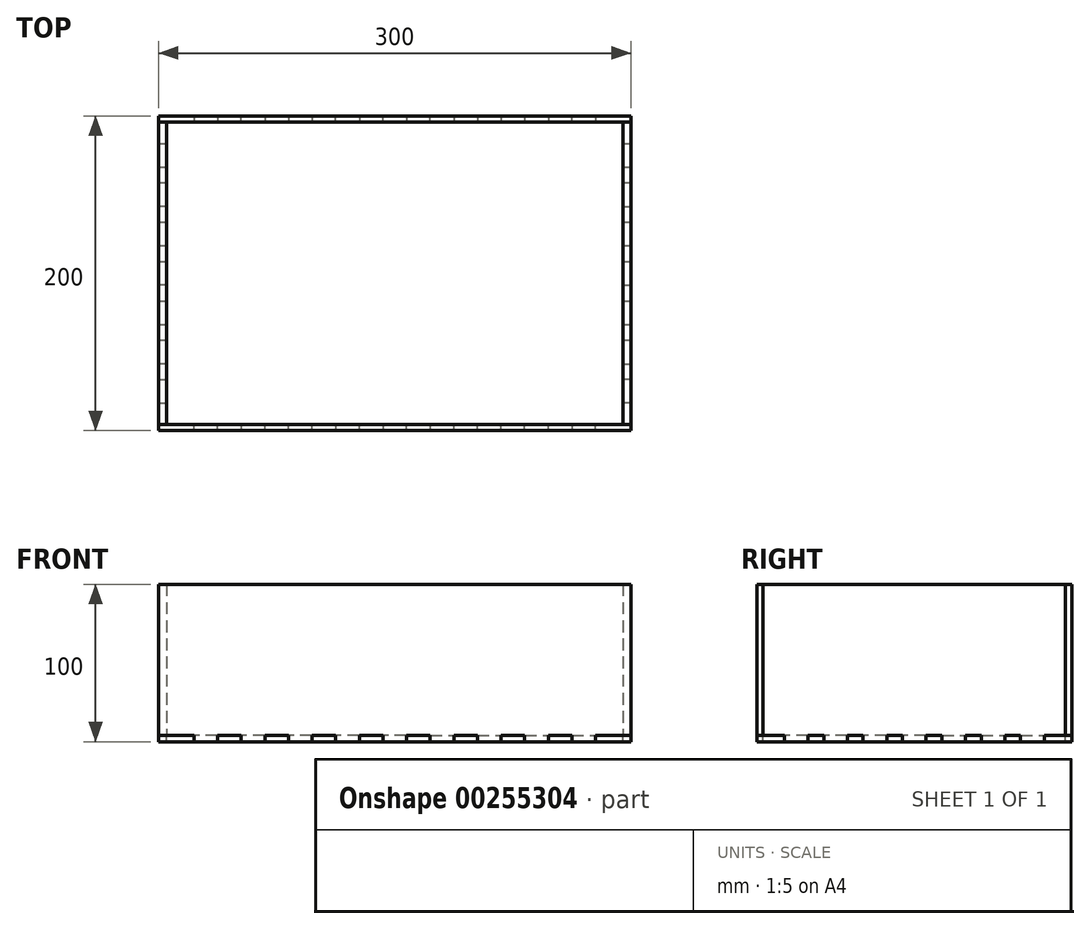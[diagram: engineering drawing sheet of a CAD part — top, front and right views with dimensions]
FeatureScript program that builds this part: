
annotation { "Feature Type Name" : "Feature", "Feature Type Description" : "" }
export const myFeature = defineFeature(function(context is Context, id is Id, definition is map)
    precondition{}
    {
        {
            var Q0;
            Q0=qCreatedBy(makeId("Top.planeOp"),FACE);
            var sketch = newSketch(context, id + "F0", { "sketchPlane" : qUnion([Q0])});
            skLineSegment(sketch, "E0.bottom", {"start": v(150, -100) * mm, "end": v(-150, -100) * mm});
            skLineSegment(sketch, "E0.top", {"start": v(150, 100) * mm, "end": v(-150, 100) * mm});
            skLineSegment(sketch, "E0.left", {"start": v(150, -100) * mm, "end": v(150, 100) * mm});
            skLineSegment(sketch, "E0.right", {"start": v(-150, -100) * mm, "end": v(-150, 100) * mm});
            skPoint(sketch, "E0.middle", {"position": v(0, 0) * mm});
            skLineSegment(sketch, "E1", {"start": v(0, 96) * mm, "end": v(7.5, 96) * mm});
            skLineSegment(sketch, "E2", {"start": v(7.5, 96) * mm, "end": v(7.5, 100) * mm});
            skLineSegment(sketch, "E3", {"start": v(0, 96) * mm, "end": v(-7.5, 96) * mm});
            skLineSegment(sketch, "E4", {"start": v(-7.5, 96) * mm, "end": v(-7.5, 100) * mm});
            skLineSegment(sketch, "E5", {"start": v(-7.5, 96) * mm, "end": v(7.5, 96) * mm});
            skPoint(sketch, "E6.start.orphan", {"position": v(0, 100) * mm});
            skLineSegment(sketch, "E7.1.0.0", {"start": v(22.5, 96) * mm, "end": v(22.5, 100) * mm});
            skLineSegment(sketch, "E7.1.0.1", {"start": v(22.5, 96) * mm, "end": v(37.5, 96) * mm});
            skLineSegment(sketch, "E7.1.0.2", {"start": v(37.5, 96) * mm, "end": v(37.5, 100) * mm});
            skLineSegment(sketch, "E7.2.0.0", {"start": v(52.5, 96) * mm, "end": v(52.5, 100) * mm});
            skLineSegment(sketch, "E7.2.0.1", {"start": v(52.5, 96) * mm, "end": v(67.5, 96) * mm});
            skLineSegment(sketch, "E7.2.0.2", {"start": v(67.5, 96) * mm, "end": v(67.5, 100) * mm});
            skLineSegment(sketch, "E7.3.0.0", {"start": v(82.5, 96) * mm, "end": v(82.5, 100) * mm});
            skLineSegment(sketch, "E7.3.0.1", {"start": v(82.5, 96) * mm, "end": v(97.5, 96) * mm});
            skLineSegment(sketch, "E7.3.0.2", {"start": v(97.5, 96) * mm, "end": v(97.5, 100) * mm});
            skLineSegment(sketch, "E7.4.0.0", {"start": v(112.5, 96) * mm, "end": v(112.5, 100) * mm});
            skLineSegment(sketch, "E7.4.0.1", {"start": v(112.5, 96) * mm, "end": v(127.5, 96) * mm});
            skLineSegment(sketch, "E7.4.0.2", {"start": v(127.5, 96) * mm, "end": v(127.5, 100) * mm});
            skLineSegment(sketch, "E7.direction1", {"start": v(-7.5, 96) * mm, "end": v(22.5, 96) * mm, "construction": true});
            skLineSegment(sketch, "E8.MirrorCS", {"start": v(-97.5, 96) * mm, "end": v(-97.5, 100) * mm});
            skLineSegment(sketch, "E9.MirrorCS", {"start": v(-67.5, 96) * mm, "end": v(-67.5, 100) * mm});
            skLineSegment(sketch, "E10.MirrorCS", {"start": v(-82.5, 96) * mm, "end": v(-82.5, 100) * mm});
            skLineSegment(sketch, "E11.MirrorCS", {"start": v(7.5, 96) * mm, "end": v(-7.5, 96) * mm});
            skLineSegment(sketch, "E12.MirrorCS", {"start": v(-22.5, 96) * mm, "end": v(-22.5, 100) * mm});
            skLineSegment(sketch, "E13.MirrorCS", {"start": v(-37.5, 96) * mm, "end": v(-37.5, 100) * mm});
            skLineSegment(sketch, "E14.MirrorCS", {"start": v(-52.5, 96) * mm, "end": v(-52.5, 100) * mm});
            skLineSegment(sketch, "E15.MirrorCS", {"start": v(-127.5, 96) * mm, "end": v(-127.5, 100) * mm});
            skLineSegment(sketch, "E16.MirrorCS", {"start": v(-112.5, 96) * mm, "end": v(-112.5, 100) * mm});
            skLineSegment(sketch, "E17.MirrorCS", {"start": v(-112.5, 96) * mm, "end": v(-127.5, 96) * mm});
            skLineSegment(sketch, "E18.MirrorCS", {"start": v(-52.5, 96) * mm, "end": v(-67.5, 96) * mm});
            skLineSegment(sketch, "E19.MirrorCS", {"start": v(7.5, 96) * mm, "end": v(-22.5, 96) * mm, "construction": true});
            skLineSegment(sketch, "E20.MirrorCS", {"start": v(-22.5, 96) * mm, "end": v(-37.5, 96) * mm});
            skLineSegment(sketch, "E21.MirrorCS", {"start": v(-82.5, 96) * mm, "end": v(-97.5, 96) * mm});
            skLineSegment(sketch, "E22.MirrorCS", {"start": v(0, -96) * mm, "end": v(-7.5, -96) * mm});
            skLineSegment(sketch, "E23.MirrorCS", {"start": v(0, -96) * mm, "end": v(7.5, -96) * mm});
            skLineSegment(sketch, "E24.MirrorCS", {"start": v(-7.5, -96) * mm, "end": v(7.5, -96) * mm});
            skLineSegment(sketch, "E25.MirrorCS", {"start": v(7.5, -96) * mm, "end": v(-7.5, -96) * mm});
            skLineSegment(sketch, "E26.MirrorCS", {"start": v(-7.5, -96) * mm, "end": v(-7.5, -100) * mm});
            skLineSegment(sketch, "E27.MirrorCS", {"start": v(7.5, -96) * mm, "end": v(7.5, -100) * mm});
            skLineSegment(sketch, "E28.MirrorCS", {"start": v(127.5, -96) * mm, "end": v(127.5, -100) * mm});
            skLineSegment(sketch, "E29.MirrorCS", {"start": v(52.5, -96) * mm, "end": v(52.5, -100) * mm});
            skLineSegment(sketch, "E30.MirrorCS", {"start": v(67.5, -96) * mm, "end": v(67.5, -100) * mm});
            skLineSegment(sketch, "E31.MirrorCS", {"start": v(82.5, -96) * mm, "end": v(82.5, -100) * mm});
            skLineSegment(sketch, "E32.MirrorCS", {"start": v(37.5, -96) * mm, "end": v(37.5, -100) * mm});
            skLineSegment(sketch, "E33.MirrorCS", {"start": v(-82.5, -96) * mm, "end": v(-82.5, -100) * mm});
            skLineSegment(sketch, "E34.MirrorCS", {"start": v(22.5, -96) * mm, "end": v(22.5, -100) * mm});
            skLineSegment(sketch, "E35.MirrorCS", {"start": v(-52.5, -96) * mm, "end": v(-52.5, -100) * mm});
            skPoint(sketch, "E36.MirrorP", {"position": v(0, -100) * mm});
            skLineSegment(sketch, "E37.MirrorCS", {"start": v(-97.5, -96) * mm, "end": v(-97.5, -100) * mm});
            skLineSegment(sketch, "E38.MirrorCS", {"start": v(-22.5, -96) * mm, "end": v(-22.5, -100) * mm});
            skLineSegment(sketch, "E39.MirrorCS", {"start": v(97.5, -96) * mm, "end": v(97.5, -100) * mm});
            skLineSegment(sketch, "E40.MirrorCS", {"start": v(-127.5, -96) * mm, "end": v(-127.5, -100) * mm});
            skLineSegment(sketch, "E41.MirrorCS", {"start": v(-67.5, -96) * mm, "end": v(-67.5, -100) * mm});
            skLineSegment(sketch, "E42.MirrorCS", {"start": v(-37.5, -96) * mm, "end": v(-37.5, -100) * mm});
            skLineSegment(sketch, "E43.MirrorCS", {"start": v(112.5, -96) * mm, "end": v(112.5, -100) * mm});
            skLineSegment(sketch, "E44.MirrorCS", {"start": v(-112.5, -96) * mm, "end": v(-112.5, -100) * mm});
            skLineSegment(sketch, "E45.MirrorCS", {"start": v(52.5, -96) * mm, "end": v(67.5, -96) * mm});
            skLineSegment(sketch, "E46.MirrorCS", {"start": v(-112.5, -96) * mm, "end": v(-127.5, -96) * mm});
            skLineSegment(sketch, "E47.MirrorCS", {"start": v(112.5, -96) * mm, "end": v(127.5, -96) * mm});
            skLineSegment(sketch, "E48.MirrorCS", {"start": v(-82.5, -96) * mm, "end": v(-97.5, -96) * mm});
            skLineSegment(sketch, "E49.MirrorCS", {"start": v(22.5, -96) * mm, "end": v(37.5, -96) * mm});
            skLineSegment(sketch, "E50.MirrorCS", {"start": v(-52.5, -96) * mm, "end": v(-67.5, -96) * mm});
            skLineSegment(sketch, "E51.MirrorCS", {"start": v(82.5, -96) * mm, "end": v(97.5, -96) * mm});
            skLineSegment(sketch, "E52.MirrorCS", {"start": v(-7.5, -96) * mm, "end": v(22.5, -96) * mm, "construction": true});
            skLineSegment(sketch, "E53.MirrorCS", {"start": v(7.5, -96) * mm, "end": v(-22.5, -96) * mm, "construction": true});
            skLineSegment(sketch, "E54.MirrorCS", {"start": v(-22.5, -96) * mm, "end": v(-37.5, -96) * mm});
            skLineSegment(sketch, "E55", {"start": v(-150, 0) * mm, "end": v(-146, 0) * mm});
            skPoint(sketch, "E55.endSnap0", {"position": v(-150, 0) * mm});
            skLineSegment(sketch, "E56", {"start": v(-145, 7.5) * mm, "end": v(-150, 7.5) * mm});
            skLineSegment(sketch, "E57", {"start": v(-145, -7.5) * mm, "end": v(-150, -7.5) * mm});
            skLineSegment(sketch, "E58", {"start": v(-145, -7.5) * mm, "end": v(-145, 7.5) * mm});
            skLineSegment(sketch, "E59.0.1.0", {"start": v(-145, 17.5) * mm, "end": v(-150, 17.5) * mm});
            skLineSegment(sketch, "E59.0.1.1", {"start": v(-145, 17.5) * mm, "end": v(-145, 32.5) * mm});
            skLineSegment(sketch, "E59.0.1.2", {"start": v(-145, 32.5) * mm, "end": v(-150, 32.5) * mm});
            skLineSegment(sketch, "E59.0.2.0", {"start": v(-145, 42.5) * mm, "end": v(-150, 42.5) * mm});
            skLineSegment(sketch, "E59.0.2.1", {"start": v(-145, 42.5) * mm, "end": v(-145, 57.5) * mm});
            skLineSegment(sketch, "E59.0.2.2", {"start": v(-145, 57.5) * mm, "end": v(-150, 57.5) * mm});
            skLineSegment(sketch, "E59.0.3.0", {"start": v(-145, 67.5) * mm, "end": v(-150, 67.5) * mm});
            skLineSegment(sketch, "E59.0.3.1", {"start": v(-145, 67.5) * mm, "end": v(-145, 82.5) * mm});
            skLineSegment(sketch, "E59.0.3.2", {"start": v(-145, 82.5) * mm, "end": v(-150, 82.5) * mm});
            skLineSegment(sketch, "E59.direction1", {"start": v(-150, -7.5) * mm, "end": v(-125, -7.5) * mm, "construction": true});
            skLineSegment(sketch, "E59.direction2", {"start": v(-150, -7.5) * mm, "end": v(-150, 17.5) * mm, "construction": true});
            skLineSegment(sketch, "E60.MirrorCS", {"start": v(-145, -17.5) * mm, "end": v(-150, -17.5) * mm});
            skLineSegment(sketch, "E61.MirrorCS", {"start": v(-145, -67.5) * mm, "end": v(-150, -67.5) * mm});
            skLineSegment(sketch, "E62.MirrorCS", {"start": v(-145, -57.5) * mm, "end": v(-150, -57.5) * mm});
            skLineSegment(sketch, "E63.MirrorCS", {"start": v(-145, -82.5) * mm, "end": v(-150, -82.5) * mm});
            skLineSegment(sketch, "E64.MirrorCS", {"start": v(-145, -42.5) * mm, "end": v(-150, -42.5) * mm});
            skLineSegment(sketch, "E65.MirrorCS", {"start": v(-145, -32.5) * mm, "end": v(-150, -32.5) * mm});
            skLineSegment(sketch, "E66.MirrorCS", {"start": v(-145, 7.5) * mm, "end": v(-145, -7.5) * mm});
            skLineSegment(sketch, "E67.MirrorCS", {"start": v(-145, -17.5) * mm, "end": v(-145, -32.5) * mm});
            skLineSegment(sketch, "E68.MirrorCS", {"start": v(-145, -67.5) * mm, "end": v(-145, -82.5) * mm});
            skLineSegment(sketch, "E69.MirrorCS", {"start": v(-150, 7.5) * mm, "end": v(-150, -17.5) * mm, "construction": true});
            skLineSegment(sketch, "E70.MirrorCS", {"start": v(-145, -42.5) * mm, "end": v(-145, -57.5) * mm});
            skLineSegment(sketch, "E71.MirrorCS", {"start": v(145, -7.5) * mm, "end": v(150, -7.5) * mm});
            skLineSegment(sketch, "E72.MirrorCS", {"start": v(145, 7.5) * mm, "end": v(150, 7.5) * mm});
            skLineSegment(sketch, "E73.MirrorCS", {"start": v(145, 7.5) * mm, "end": v(145, -7.5) * mm});
            skLineSegment(sketch, "E74.MirrorCS", {"start": v(150, 0) * mm, "end": v(146, 0) * mm});
            skLineSegment(sketch, "E75.MirrorCS", {"start": v(145, -7.5) * mm, "end": v(145, 7.5) * mm});
            skLineSegment(sketch, "E76.MirrorCS", {"start": v(145, -17.5) * mm, "end": v(150, -17.5) * mm});
            skLineSegment(sketch, "E77.MirrorCS", {"start": v(145, 17.5) * mm, "end": v(150, 17.5) * mm});
            skLineSegment(sketch, "E78.MirrorCS", {"start": v(145, 57.5) * mm, "end": v(150, 57.5) * mm});
            skLineSegment(sketch, "E79.MirrorCS", {"start": v(145, 67.5) * mm, "end": v(150, 67.5) * mm});
            skLineSegment(sketch, "E80.MirrorCS", {"start": v(145, -67.5) * mm, "end": v(150, -67.5) * mm});
            skLineSegment(sketch, "E81.MirrorCS", {"start": v(145, 82.5) * mm, "end": v(150, 82.5) * mm});
            skLineSegment(sketch, "E82.MirrorCS", {"start": v(145, -57.5) * mm, "end": v(150, -57.5) * mm});
            skPoint(sketch, "E83.MirrorP", {"position": v(150, 0) * mm});
            skLineSegment(sketch, "E84.MirrorCS", {"start": v(145, 42.5) * mm, "end": v(150, 42.5) * mm});
            skLineSegment(sketch, "E85.MirrorCS", {"start": v(145, -32.5) * mm, "end": v(150, -32.5) * mm});
            skLineSegment(sketch, "E86.MirrorCS", {"start": v(145, 32.5) * mm, "end": v(150, 32.5) * mm});
            skLineSegment(sketch, "E87.MirrorCS", {"start": v(145, -42.5) * mm, "end": v(150, -42.5) * mm});
            skLineSegment(sketch, "E88.MirrorCS", {"start": v(145, -82.5) * mm, "end": v(150, -82.5) * mm});
            skLineSegment(sketch, "E89.MirrorCS", {"start": v(145, -42.5) * mm, "end": v(145, -57.5) * mm});
            skLineSegment(sketch, "E90.MirrorCS", {"start": v(145, -17.5) * mm, "end": v(145, -32.5) * mm});
            skLineSegment(sketch, "E91.MirrorCS", {"start": v(145, 42.5) * mm, "end": v(145, 57.5) * mm});
            skLineSegment(sketch, "E92.MirrorCS", {"start": v(145, -67.5) * mm, "end": v(145, -82.5) * mm});
            skLineSegment(sketch, "E93.MirrorCS", {"start": v(150, 7.5) * mm, "end": v(150, -17.5) * mm, "construction": true});
            skLineSegment(sketch, "E94.MirrorCS", {"start": v(145, 67.5) * mm, "end": v(145, 82.5) * mm});
            skLineSegment(sketch, "E95.MirrorCS", {"start": v(150, -7.5) * mm, "end": v(150, 17.5) * mm, "construction": true});
            skLineSegment(sketch, "E96.MirrorCS", {"start": v(145, 17.5) * mm, "end": v(145, 32.5) * mm});
            skSolve(sketch);
        }
        {
            var Q0;
            {var subQ54=sQuery(id+"F0.wireOp",EDGE,"E7.1.0.0");Q0=makeQuery(id+"F0.imprint","IMPRINT",FACE,{"disambiguationData":[TD([[makeQuery(id+"F0.imprint","IMPRINT",EDGE,{"derivedFrom":subQ54}),1.0]])]});}
            extrude(context, id + "F1", {"entities" : qUnion([Q0]), "depth" : 4 * mm});
        }
        {
            var Q0;
            Q0=makeQuery(id+"F1.opExtrude","CAP_FACE",FACE,{"disambiguationData":[OSD([sQuery(id+"F0.wireOp",EDGE,"E0.bottom"),sQuery(id+"F0.wireOp",EDGE,"E0.top"),sQuery(id+"F0.wireOp",EDGE,"E0.left"),sQuery(id+"F0.wireOp",EDGE,"E0.right"),sQuery(id+"F0.wireOp",EDGE,"E7.1.0.0"),sQuery(id+"F0.wireOp",EDGE,"E7.1.0.1"),sQuery(id+"F0.wireOp",EDGE,"E7.1.0.2"),sQuery(id+"F0.wireOp",EDGE,"E7.2.0.0"),sQuery(id+"F0.wireOp",EDGE,"E7.2.0.1"),sQuery(id+"F0.wireOp",EDGE,"E7.2.0.2"),sQuery(id+"F0.wireOp",EDGE,"E7.3.0.0"),sQuery(id+"F0.wireOp",EDGE,"E7.3.0.1"),sQuery(id+"F0.wireOp",EDGE,"E7.3.0.2"),sQuery(id+"F0.wireOp",EDGE,"E7.4.0.0"),sQuery(id+"F0.wireOp",EDGE,"E7.4.0.1"),sQuery(id+"F0.wireOp",EDGE,"E7.4.0.2"),sQuery(id+"F0.wireOp",EDGE,"E8.MirrorCS"),sQuery(id+"F0.wireOp",EDGE,"E9.MirrorCS"),sQuery(id+"F0.wireOp",EDGE,"E10.MirrorCS"),sQuery(id+"F0.wireOp",EDGE,"E4"),sQuery(id+"F0.wireOp",EDGE,"E2"),sQuery(id+"F0.wireOp",EDGE,"E11.MirrorCS"),sQuery(id+"F0.wireOp",EDGE,"E12.MirrorCS"),sQuery(id+"F0.wireOp",EDGE,"E13.MirrorCS"),sQuery(id+"F0.wireOp",EDGE,"E14.MirrorCS"),sQuery(id+"F0.wireOp",EDGE,"E15.MirrorCS"),sQuery(id+"F0.wireOp",EDGE,"E16.MirrorCS"),sQuery(id+"F0.wireOp",EDGE,"E17.MirrorCS"),sQuery(id+"F0.wireOp",EDGE,"E18.MirrorCS"),sQuery(id+"F0.wireOp",EDGE,"E20.MirrorCS"),sQuery(id+"F0.wireOp",EDGE,"E21.MirrorCS"),sQuery(id+"F0.wireOp",EDGE,"E25.MirrorCS"),sQuery(id+"F0.wireOp",EDGE,"E22.MirrorCS"),sQuery(id+"F0.wireOp",EDGE,"E26.MirrorCS"),sQuery(id+"F0.wireOp",EDGE,"E27.MirrorCS"),sQuery(id+"F0.wireOp",EDGE,"E28.MirrorCS"),sQuery(id+"F0.wireOp",EDGE,"E29.MirrorCS"),sQuery(id+"F0.wireOp",EDGE,"E30.MirrorCS"),sQuery(id+"F0.wireOp",EDGE,"E31.MirrorCS"),sQuery(id+"F0.wireOp",EDGE,"E32.MirrorCS"),sQuery(id+"F0.wireOp",EDGE,"E33.MirrorCS"),sQuery(id+"F0.wireOp",EDGE,"E34.MirrorCS"),sQuery(id+"F0.wireOp",EDGE,"E35.MirrorCS"),sQuery(id+"F0.wireOp",EDGE,"E37.MirrorCS"),sQuery(id+"F0.wireOp",EDGE,"E38.MirrorCS"),sQuery(id+"F0.wireOp",EDGE,"E39.MirrorCS"),sQuery(id+"F0.wireOp",EDGE,"E40.MirrorCS"),sQuery(id+"F0.wireOp",EDGE,"E41.MirrorCS"),sQuery(id+"F0.wireOp",EDGE,"E42.MirrorCS"),sQuery(id+"F0.wireOp",EDGE,"E43.MirrorCS"),sQuery(id+"F0.wireOp",EDGE,"E44.MirrorCS"),sQuery(id+"F0.wireOp",EDGE,"E45.MirrorCS"),sQuery(id+"F0.wireOp",EDGE,"E46.MirrorCS"),sQuery(id+"F0.wireOp",EDGE,"E47.MirrorCS"),sQuery(id+"F0.wireOp",EDGE,"E48.MirrorCS"),sQuery(id+"F0.wireOp",EDGE,"E49.MirrorCS"),sQuery(id+"F0.wireOp",EDGE,"E50.MirrorCS"),sQuery(id+"F0.wireOp",EDGE,"E51.MirrorCS"),sQuery(id+"F0.wireOp",EDGE,"E54.MirrorCS"),sQuery(id+"F0.wireOp",EDGE,"E59.0.1.0"),sQuery(id+"F0.wireOp",EDGE,"E59.0.1.1"),sQuery(id+"F0.wireOp",EDGE,"E59.0.1.2"),sQuery(id+"F0.wireOp",EDGE,"E59.0.2.0"),sQuery(id+"F0.wireOp",EDGE,"E59.0.2.1"),sQuery(id+"F0.wireOp",EDGE,"E59.0.2.2"),sQuery(id+"F0.wireOp",EDGE,"E59.0.3.0"),sQuery(id+"F0.wireOp",EDGE,"E59.0.3.1"),sQuery(id+"F0.wireOp",EDGE,"E59.0.3.2"),sQuery(id+"F0.wireOp",EDGE,"E60.MirrorCS"),sQuery(id+"F0.wireOp",EDGE,"E56"),sQuery(id+"F0.wireOp",EDGE,"E61.MirrorCS"),sQuery(id+"F0.wireOp",EDGE,"E62.MirrorCS"),sQuery(id+"F0.wireOp",EDGE,"E57"),sQuery(id+"F0.wireOp",EDGE,"E63.MirrorCS"),sQuery(id+"F0.wireOp",EDGE,"E64.MirrorCS"),sQuery(id+"F0.wireOp",EDGE,"E65.MirrorCS"),sQuery(id+"F0.wireOp",EDGE,"E66.MirrorCS"),sQuery(id+"F0.wireOp",EDGE,"E67.MirrorCS"),sQuery(id+"F0.wireOp",EDGE,"E68.MirrorCS"),sQuery(id+"F0.wireOp",EDGE,"E70.MirrorCS"),sQuery(id+"F0.wireOp",EDGE,"E71.MirrorCS"),sQuery(id+"F0.wireOp",EDGE,"E72.MirrorCS"),sQuery(id+"F0.wireOp",EDGE,"E75.MirrorCS"),sQuery(id+"F0.wireOp",EDGE,"E76.MirrorCS"),sQuery(id+"F0.wireOp",EDGE,"E77.MirrorCS"),sQuery(id+"F0.wireOp",EDGE,"E78.MirrorCS"),sQuery(id+"F0.wireOp",EDGE,"E79.MirrorCS"),sQuery(id+"F0.wireOp",EDGE,"E80.MirrorCS"),sQuery(id+"F0.wireOp",EDGE,"E81.MirrorCS"),sQuery(id+"F0.wireOp",EDGE,"E82.MirrorCS"),sQuery(id+"F0.wireOp",EDGE,"E84.MirrorCS"),sQuery(id+"F0.wireOp",EDGE,"E85.MirrorCS"),sQuery(id+"F0.wireOp",EDGE,"E86.MirrorCS"),sQuery(id+"F0.wireOp",EDGE,"E87.MirrorCS"),sQuery(id+"F0.wireOp",EDGE,"E88.MirrorCS"),sQuery(id+"F0.wireOp",EDGE,"E89.MirrorCS"),sQuery(id+"F0.wireOp",EDGE,"E90.MirrorCS"),sQuery(id+"F0.wireOp",EDGE,"E91.MirrorCS"),sQuery(id+"F0.wireOp",EDGE,"E92.MirrorCS"),sQuery(id+"F0.wireOp",EDGE,"E94.MirrorCS"),sQuery(id+"F0.wireOp",EDGE,"E96.MirrorCS")])],"isStart":false});
            var sketch = newSketch(context, id + "F2", { "sketchPlane" : qUnion([Q0])});
            skLineSegment(sketch, "E97.2", {"start": v(-82.5, 96) * mm, "end": v(-82.5, 100) * mm});
            skLineSegment(sketch, "E97.4", {"start": v(-112.5, 96) * mm, "end": v(-112.5, 100) * mm});
            skLineSegment(sketch, "E97.6", {"start": v(82.5, 96) * mm, "end": v(82.5, 100) * mm});
            skLineSegment(sketch, "E97.7", {"start": v(-97.5, 100) * mm, "end": v(-112.5, 100) * mm});
            skLineSegment(sketch, "E97.10", {"start": v(-97.5, 96) * mm, "end": v(-97.5, 100) * mm});
            skLineSegment(sketch, "E97.11", {"start": v(-52.5, 96) * mm, "end": v(-52.5, 100) * mm});
            skLineSegment(sketch, "E97.12", {"start": v(-7.5, 96) * mm, "end": v(-7.5, 100) * mm});
            skLineSegment(sketch, "E97.13", {"start": v(82.5, 96) * mm, "end": v(97.5, 96) * mm});
            skLineSegment(sketch, "E97.14", {"start": v(52.5, 96) * mm, "end": v(52.5, 100) * mm});
            skLineSegment(sketch, "E97.16", {"start": v(-37.5, 96) * mm, "end": v(-37.5, 100) * mm});
            skLineSegment(sketch, "E97.19", {"start": v(-112.5, 96) * mm, "end": v(-127.5, 96) * mm});
            skLineSegment(sketch, "E97.20", {"start": v(-127.5, 96) * mm, "end": v(-127.5, 100) * mm});
            skLineSegment(sketch, "E97.21", {"start": v(67.5, 96) * mm, "end": v(67.5, 100) * mm});
            skLineSegment(sketch, "E97.22", {"start": v(-67.5, 96) * mm, "end": v(-67.5, 100) * mm});
            skLineSegment(sketch, "E97.24", {"start": v(22.5, 96) * mm, "end": v(22.5, 100) * mm});
            skLineSegment(sketch, "E97.25", {"start": v(97.5, 96) * mm, "end": v(97.5, 100) * mm});
            skLineSegment(sketch, "E97.26", {"start": v(7.5, 96) * mm, "end": v(7.5, 100) * mm});
            skLineSegment(sketch, "E97.27", {"start": v(-52.5, 96) * mm, "end": v(-67.5, 96) * mm});
            skLineSegment(sketch, "E97.29", {"start": v(37.5, 96) * mm, "end": v(37.5, 100) * mm});
            skLineSegment(sketch, "E97.30", {"start": v(112.5, 96) * mm, "end": v(127.5, 96) * mm});
            skLineSegment(sketch, "E97.31", {"start": v(52.5, 100) * mm, "end": v(37.5, 100) * mm});
            skLineSegment(sketch, "E97.32", {"start": v(22.5, 96) * mm, "end": v(37.5, 96) * mm});
            skLineSegment(sketch, "E97.33", {"start": v(112.5, 96) * mm, "end": v(112.5, 100) * mm});
            skLineSegment(sketch, "E97.34", {"start": v(127.5, 96) * mm, "end": v(127.5, 100) * mm});
            skLineSegment(sketch, "E97.35", {"start": v(52.5, 96) * mm, "end": v(67.5, 96) * mm});
            skLineSegment(sketch, "E97.36", {"start": v(7.5, 96) * mm, "end": v(-7.5, 96) * mm});
            skLineSegment(sketch, "E97.37", {"start": v(-22.5, 96) * mm, "end": v(-37.5, 96) * mm});
            skLineSegment(sketch, "E97.38", {"start": v(22.5, 100) * mm, "end": v(7.5, 100) * mm});
            skLineSegment(sketch, "E97.39", {"start": v(-22.5, 96) * mm, "end": v(-22.5, 100) * mm});
            skLineSegment(sketch, "E97.40", {"start": v(-82.5, 96) * mm, "end": v(-97.5, 96) * mm});
            skLineSegment(sketch, "E97.42", {"start": v(67.5, 96) * mm, "end": v(67.5, 100) * mm});
            skLineSegment(sketch, "E97.43", {"start": v(-97.5, 96) * mm, "end": v(-97.5, 100) * mm});
            skLineSegment(sketch, "E97.47", {"start": v(-67.5, 96) * mm, "end": v(-67.5, 100) * mm});
            skLineSegment(sketch, "E97.48", {"start": v(82.5, 96) * mm, "end": v(82.5, 100) * mm});
            skLineSegment(sketch, "E97.50", {"start": v(52.5, 96) * mm, "end": v(67.5, 96) * mm});
            skLineSegment(sketch, "E97.55", {"start": v(-67.5, 100) * mm, "end": v(-82.5, 100) * mm});
            skLineSegment(sketch, "E97.56", {"start": v(-7.5, 96) * mm, "end": v(-7.5, 100) * mm});
            skLineSegment(sketch, "E97.57", {"start": v(82.5, 96) * mm, "end": v(97.5, 96) * mm});
            skLineSegment(sketch, "E97.58", {"start": v(112.5, 100) * mm, "end": v(97.5, 100) * mm});
            skLineSegment(sketch, "E97.59", {"start": v(-112.5, 96) * mm, "end": v(-127.5, 96) * mm});
            skLineSegment(sketch, "E97.60", {"start": v(-127.5, 96) * mm, "end": v(-127.5, 100) * mm});
            skLineSegment(sketch, "E97.61", {"start": v(-52.5, 96) * mm, "end": v(-67.5, 96) * mm});
            skLineSegment(sketch, "E97.64", {"start": v(97.5, 96) * mm, "end": v(97.5, 100) * mm});
            skLineSegment(sketch, "E97.71", {"start": v(82.5, 100) * mm, "end": v(67.5, 100) * mm});
            skLineSegment(sketch, "E97.72", {"start": v(22.5, 96) * mm, "end": v(22.5, 100) * mm});
            skLineSegment(sketch, "E97.74", {"start": v(-82.5, 96) * mm, "end": v(-82.5, 100) * mm});
            skLineSegment(sketch, "E97.75", {"start": v(-112.5, 96) * mm, "end": v(-112.5, 100) * mm});
            skLineSegment(sketch, "E97.78", {"start": v(22.5, 96) * mm, "end": v(37.5, 96) * mm});
            skLineSegment(sketch, "E97.79", {"start": v(112.5, 96) * mm, "end": v(112.5, 100) * mm});
            skLineSegment(sketch, "E97.80", {"start": v(7.5, 96) * mm, "end": v(-7.5, 96) * mm});
            skLineSegment(sketch, "E97.81", {"start": v(-22.5, 96) * mm, "end": v(-37.5, 96) * mm});
            skLineSegment(sketch, "E97.84", {"start": v(22.5, 100) * mm, "end": v(7.5, 100) * mm});
            skLineSegment(sketch, "E97.85", {"start": v(37.5, 96) * mm, "end": v(37.5, 100) * mm});
            skLineSegment(sketch, "E97.86", {"start": v(112.5, 96) * mm, "end": v(127.5, 96) * mm});
            skLineSegment(sketch, "E97.87", {"start": v(-82.5, 96) * mm, "end": v(-97.5, 96) * mm});
            skLineSegment(sketch, "E97.90", {"start": v(-37.5, 96) * mm, "end": v(-37.5, 100) * mm});
            skLineSegment(sketch, "E97.91", {"start": v(52.5, 96) * mm, "end": v(52.5, 100) * mm});
            skLineSegment(sketch, "E97.92", {"start": v(127.5, 96) * mm, "end": v(127.5, 100) * mm});
            skLineSegment(sketch, "E97.95", {"start": v(-7.5, 100) * mm, "end": v(-22.5, 100) * mm});
            skLineSegment(sketch, "E97.98", {"start": v(-52.5, 96) * mm, "end": v(-52.5, 100) * mm});
            skLineSegment(sketch, "E97.99", {"start": v(-37.5, 100) * mm, "end": v(-52.5, 100) * mm});
            skLineSegment(sketch, "E97.100", {"start": v(7.5, 96) * mm, "end": v(7.5, 100) * mm});
            skLineSegment(sketch, "E97.104", {"start": v(-22.5, 96) * mm, "end": v(-22.5, 100) * mm});
            skLineSegment(sketch, "E98", {"start": v(-127.5, 100) * mm, "end": v(-112.5, 100) * mm});
            skLineSegment(sketch, "E99.trimOffspring", {"start": v(-7.5, 100) * mm, "end": v(7.5, 100) * mm});
            skLineSegment(sketch, "E100.trimOffspring", {"start": v(-37.5, 100) * mm, "end": v(-22.5, 100) * mm});
            skLineSegment(sketch, "E101.trimOffspring", {"start": v(-97.5, 100) * mm, "end": v(-82.5, 100) * mm});
            skLineSegment(sketch, "E102.trimOffspring", {"start": v(-67.5, 100) * mm, "end": v(-52.5, 100) * mm});
            skLineSegment(sketch, "E103.trimOffspring", {"start": v(22.5, 100) * mm, "end": v(127.5, 100) * mm});
            skLineSegment(sketch, "E104.MirrorCS", {"start": v(-97.5, -96) * mm, "end": v(-97.5, -100) * mm});
            skLineSegment(sketch, "E105.MirrorCS", {"start": v(-112.5, -96) * mm, "end": v(-112.5, -100) * mm});
            skLineSegment(sketch, "E106.MirrorCS", {"start": v(7.5, -96) * mm, "end": v(7.5, -100) * mm});
            skLineSegment(sketch, "E107.MirrorCS", {"start": v(22.5, -96) * mm, "end": v(22.5, -100) * mm});
            skLineSegment(sketch, "E108.MirrorCS", {"start": v(-52.5, -96) * mm, "end": v(-52.5, -100) * mm});
            skLineSegment(sketch, "E109.MirrorCS", {"start": v(-7.5, -96) * mm, "end": v(-7.5, -100) * mm});
            skLineSegment(sketch, "E110.MirrorCS", {"start": v(-67.5, -96) * mm, "end": v(-67.5, -100) * mm});
            skLineSegment(sketch, "E111.MirrorCS", {"start": v(-22.5, -96) * mm, "end": v(-22.5, -100) * mm});
            skLineSegment(sketch, "E112.MirrorCS", {"start": v(-37.5, -96) * mm, "end": v(-37.5, -100) * mm});
            skLineSegment(sketch, "E113.MirrorCS", {"start": v(-82.5, -96) * mm, "end": v(-82.5, -100) * mm});
            skLineSegment(sketch, "E114.MirrorCS", {"start": v(37.5, -96) * mm, "end": v(37.5, -100) * mm});
            skLineSegment(sketch, "E115.MirrorCS", {"start": v(52.5, -96) * mm, "end": v(52.5, -100) * mm});
            skLineSegment(sketch, "E116.MirrorCS", {"start": v(97.5, -96) * mm, "end": v(97.5, -100) * mm});
            skLineSegment(sketch, "E117.MirrorCS", {"start": v(-127.5, -96) * mm, "end": v(-127.5, -100) * mm});
            skLineSegment(sketch, "E118.MirrorCS", {"start": v(82.5, -96) * mm, "end": v(82.5, -100) * mm});
            skLineSegment(sketch, "E119.MirrorCS", {"start": v(127.5, -96) * mm, "end": v(127.5, -100) * mm});
            skLineSegment(sketch, "E120.MirrorCS", {"start": v(112.5, -96) * mm, "end": v(112.5, -100) * mm});
            skLineSegment(sketch, "E121.MirrorCS", {"start": v(67.5, -96) * mm, "end": v(67.5, -100) * mm});
            skLineSegment(sketch, "E122.MirrorCS", {"start": v(-112.5, -96) * mm, "end": v(-127.5, -96) * mm});
            skLineSegment(sketch, "E123.MirrorCS", {"start": v(22.5, -96) * mm, "end": v(37.5, -96) * mm});
            skLineSegment(sketch, "E124.MirrorCS", {"start": v(82.5, -96) * mm, "end": v(97.5, -96) * mm});
            skLineSegment(sketch, "E125.MirrorCS", {"start": v(-82.5, -96) * mm, "end": v(-97.5, -96) * mm});
            skLineSegment(sketch, "E126.MirrorCS", {"start": v(7.5, -96) * mm, "end": v(-7.5, -96) * mm});
            skLineSegment(sketch, "E127.MirrorCS", {"start": v(112.5, -96) * mm, "end": v(127.5, -96) * mm});
            skLineSegment(sketch, "E128.MirrorCS", {"start": v(-52.5, -96) * mm, "end": v(-67.5, -96) * mm});
            skLineSegment(sketch, "E129.MirrorCS", {"start": v(-22.5, -96) * mm, "end": v(-37.5, -96) * mm});
            skLineSegment(sketch, "E130.MirrorCS", {"start": v(82.5, -100) * mm, "end": v(67.5, -100) * mm});
            skLineSegment(sketch, "E131.MirrorCS", {"start": v(52.5, -100) * mm, "end": v(37.5, -100) * mm});
            skLineSegment(sketch, "E132.MirrorCS", {"start": v(22.5, -100) * mm, "end": v(7.5, -100) * mm});
            skLineSegment(sketch, "E133.MirrorCS", {"start": v(52.5, -96) * mm, "end": v(67.5, -96) * mm});
            skLineSegment(sketch, "E134.MirrorCS", {"start": v(-7.5, -100) * mm, "end": v(7.5, -100) * mm});
            skLineSegment(sketch, "E135.MirrorCS", {"start": v(-127.5, -100) * mm, "end": v(-112.5, -100) * mm});
            skLineSegment(sketch, "E136.MirrorCS", {"start": v(112.5, -100) * mm, "end": v(97.5, -100) * mm});
            skLineSegment(sketch, "E137.MirrorCS", {"start": v(-67.5, -100) * mm, "end": v(-52.5, -100) * mm});
            skLineSegment(sketch, "E138.MirrorCS", {"start": v(-67.5, -100) * mm, "end": v(-82.5, -100) * mm});
            skLineSegment(sketch, "E139.MirrorCS", {"start": v(-7.5, -100) * mm, "end": v(-22.5, -100) * mm});
            skLineSegment(sketch, "E140.MirrorCS", {"start": v(22.5, -100) * mm, "end": v(127.5, -100) * mm});
            skLineSegment(sketch, "E141.MirrorCS", {"start": v(-37.5, -100) * mm, "end": v(-52.5, -100) * mm});
            skLineSegment(sketch, "E142.MirrorCS", {"start": v(-37.5, -100) * mm, "end": v(-22.5, -100) * mm});
            skLineSegment(sketch, "E143.MirrorCS", {"start": v(-97.5, -100) * mm, "end": v(-112.5, -100) * mm});
            skLineSegment(sketch, "E144.MirrorCS", {"start": v(-97.5, -100) * mm, "end": v(-82.5, -100) * mm});
            skLineSegment(sketch, "E145.0", {"start": v(-150, -17.5) * mm, "end": v(-150, -7.5) * mm});
            skLineSegment(sketch, "E145.1", {"start": v(-150, 57.5) * mm, "end": v(-150, 67.5) * mm});
            skLineSegment(sketch, "E145.2", {"start": v(-145, -32.5) * mm, "end": v(-150, -32.5) * mm});
            skLineSegment(sketch, "E145.3", {"start": v(-145, 17.5) * mm, "end": v(-150, 17.5) * mm});
            skLineSegment(sketch, "E145.4", {"start": v(-145, 82.5) * mm, "end": v(-150, 82.5) * mm});
            skLineSegment(sketch, "E145.5", {"start": v(-150, 7.5) * mm, "end": v(-150, 17.5) * mm});
            skLineSegment(sketch, "E145.6", {"start": v(-145, -17.5) * mm, "end": v(-150, -17.5) * mm});
            skLineSegment(sketch, "E145.7", {"start": v(-145, 7.5) * mm, "end": v(-145, -7.5) * mm});
            skLineSegment(sketch, "E145.8", {"start": v(-145, 67.5) * mm, "end": v(-150, 67.5) * mm});
            skLineSegment(sketch, "E145.9", {"start": v(-145, -82.5) * mm, "end": v(-150, -82.5) * mm});
            skLineSegment(sketch, "E145.10", {"start": v(-145, 57.5) * mm, "end": v(-150, 57.5) * mm});
            skLineSegment(sketch, "E145.11", {"start": v(-145, 17.5) * mm, "end": v(-145, 32.5) * mm});
            skLineSegment(sketch, "E145.12", {"start": v(-150, 32.5) * mm, "end": v(-150, 42.5) * mm});
            skLineSegment(sketch, "E145.13", {"start": v(-145, 67.5) * mm, "end": v(-145, 82.5) * mm});
            skLineSegment(sketch, "E145.14", {"start": v(-145, -42.5) * mm, "end": v(-150, -42.5) * mm});
            skLineSegment(sketch, "E145.15", {"start": v(-145, 7.5) * mm, "end": v(-150, 7.5) * mm});
            skLineSegment(sketch, "E145.16", {"start": v(-145, -17.5) * mm, "end": v(-145, -32.5) * mm});
            skLineSegment(sketch, "E145.17", {"start": v(-145, 32.5) * mm, "end": v(-150, 32.5) * mm});
            skLineSegment(sketch, "E145.18", {"start": v(-150, -42.5) * mm, "end": v(-150, -32.5) * mm});
            skLineSegment(sketch, "E145.19", {"start": v(-150, -67.5) * mm, "end": v(-150, -57.5) * mm});
            skLineSegment(sketch, "E145.20", {"start": v(-145, -42.5) * mm, "end": v(-145, -57.5) * mm});
            skLineSegment(sketch, "E145.21", {"start": v(-145, 42.5) * mm, "end": v(-145, 57.5) * mm});
            skLineSegment(sketch, "E145.22", {"start": v(-145, -57.5) * mm, "end": v(-150, -57.5) * mm});
            skLineSegment(sketch, "E145.23", {"start": v(-145, -7.5) * mm, "end": v(-150, -7.5) * mm});
            skLineSegment(sketch, "E145.24", {"start": v(-145, -67.5) * mm, "end": v(-145, -82.5) * mm});
            skLineSegment(sketch, "E145.25", {"start": v(-145, -67.5) * mm, "end": v(-150, -67.5) * mm});
            skLineSegment(sketch, "E145.26", {"start": v(-145, 42.5) * mm, "end": v(-150, 42.5) * mm});
            skLineSegment(sketch, "E145.30", {"start": v(-150, 32.5) * mm, "end": v(-150, 42.5) * mm});
            skLineSegment(sketch, "E145.32", {"start": v(-145, 82.5) * mm, "end": v(-150, 82.5) * mm});
            skLineSegment(sketch, "E145.33", {"start": v(-145, 67.5) * mm, "end": v(-150, 67.5) * mm});
            skLineSegment(sketch, "E145.34", {"start": v(-145, -17.5) * mm, "end": v(-150, -17.5) * mm});
            skLineSegment(sketch, "E145.35", {"start": v(-145, 17.5) * mm, "end": v(-145, 32.5) * mm});
            skLineSegment(sketch, "E145.37", {"start": v(-145, -82.5) * mm, "end": v(-150, -82.5) * mm});
            skLineSegment(sketch, "E145.42", {"start": v(-150, 57.5) * mm, "end": v(-150, 67.5) * mm});
            skLineSegment(sketch, "E145.44", {"start": v(-145, 17.5) * mm, "end": v(-150, 17.5) * mm});
            skLineSegment(sketch, "E145.45", {"start": v(-145, 32.5) * mm, "end": v(-150, 32.5) * mm});
            skLineSegment(sketch, "E145.47", {"start": v(-145, 7.5) * mm, "end": v(-145, -7.5) * mm});
            skLineSegment(sketch, "E145.49", {"start": v(-145, -17.5) * mm, "end": v(-145, -32.5) * mm});
            skLineSegment(sketch, "E145.51", {"start": v(-145, 7.5) * mm, "end": v(-150, 7.5) * mm});
            skLineSegment(sketch, "E145.53", {"start": v(-145, -32.5) * mm, "end": v(-150, -32.5) * mm});
            skLineSegment(sketch, "E145.54", {"start": v(-145, 42.5) * mm, "end": v(-150, 42.5) * mm});
            skLineSegment(sketch, "E145.55", {"start": v(-145, -67.5) * mm, "end": v(-150, -67.5) * mm});
            skLineSegment(sketch, "E145.60", {"start": v(-150, -67.5) * mm, "end": v(-150, -57.5) * mm});
            skLineSegment(sketch, "E145.61", {"start": v(-145, -67.5) * mm, "end": v(-145, -82.5) * mm});
            skLineSegment(sketch, "E145.62", {"start": v(-145, 42.5) * mm, "end": v(-145, 57.5) * mm});
            skLineSegment(sketch, "E145.65", {"start": v(-145, 57.5) * mm, "end": v(-150, 57.5) * mm});
            skLineSegment(sketch, "E145.66", {"start": v(-145, -7.5) * mm, "end": v(-150, -7.5) * mm});
            skLineSegment(sketch, "E145.67", {"start": v(-150, -17.5) * mm, "end": v(-150, -7.5) * mm});
            skLineSegment(sketch, "E145.72", {"start": v(-150, 7.5) * mm, "end": v(-150, 17.5) * mm});
            skLineSegment(sketch, "E145.75", {"start": v(-145, -42.5) * mm, "end": v(-150, -42.5) * mm});
            skLineSegment(sketch, "E145.76", {"start": v(-145, 67.5) * mm, "end": v(-145, 82.5) * mm});
            skLineSegment(sketch, "E145.77", {"start": v(-150, -42.5) * mm, "end": v(-150, -32.5) * mm});
            skLineSegment(sketch, "E145.80", {"start": v(-145, -42.5) * mm, "end": v(-145, -57.5) * mm});
            skLineSegment(sketch, "E145.81", {"start": v(-145, -57.5) * mm, "end": v(-150, -57.5) * mm});
            skLineSegment(sketch, "E146", {"start": v(-150, 82.5) * mm, "end": v(-150, -82.5) * mm});
            skLineSegment(sketch, "E147.MirrorCS", {"start": v(145, -42.5) * mm, "end": v(150, -42.5) * mm});
            skLineSegment(sketch, "E148.MirrorCS", {"start": v(145, 32.5) * mm, "end": v(150, 32.5) * mm});
            skLineSegment(sketch, "E149.MirrorCS", {"start": v(145, 17.5) * mm, "end": v(150, 17.5) * mm});
            skLineSegment(sketch, "E150.MirrorCS", {"start": v(145, -32.5) * mm, "end": v(150, -32.5) * mm});
            skLineSegment(sketch, "E151.MirrorCS", {"start": v(145, 67.5) * mm, "end": v(150, 67.5) * mm});
            skLineSegment(sketch, "E152.MirrorCS", {"start": v(145, -17.5) * mm, "end": v(150, -17.5) * mm});
            skLineSegment(sketch, "E153.MirrorCS", {"start": v(145, -67.5) * mm, "end": v(150, -67.5) * mm});
            skLineSegment(sketch, "E154.MirrorCS", {"start": v(145, -57.5) * mm, "end": v(150, -57.5) * mm});
            skLineSegment(sketch, "E155.MirrorCS", {"start": v(145, 57.5) * mm, "end": v(150, 57.5) * mm});
            skLineSegment(sketch, "E156.MirrorCS", {"start": v(145, 42.5) * mm, "end": v(150, 42.5) * mm});
            skLineSegment(sketch, "E157.MirrorCS", {"start": v(145, 7.5) * mm, "end": v(150, 7.5) * mm});
            skLineSegment(sketch, "E158.MirrorCS", {"start": v(145, -7.5) * mm, "end": v(150, -7.5) * mm});
            skLineSegment(sketch, "E159.MirrorCS", {"start": v(145, 82.5) * mm, "end": v(150, 82.5) * mm});
            skLineSegment(sketch, "E160.MirrorCS", {"start": v(145, -82.5) * mm, "end": v(150, -82.5) * mm});
            skLineSegment(sketch, "E161.MirrorCS", {"start": v(150, 57.5) * mm, "end": v(150, 67.5) * mm});
            skLineSegment(sketch, "E162.MirrorCS", {"start": v(150, -42.5) * mm, "end": v(150, -32.5) * mm});
            skLineSegment(sketch, "E163.MirrorCS", {"start": v(150, -67.5) * mm, "end": v(150, -57.5) * mm});
            skLineSegment(sketch, "E164.MirrorCS", {"start": v(145, 67.5) * mm, "end": v(145, 82.5) * mm});
            skLineSegment(sketch, "E165.MirrorCS", {"start": v(145, -42.5) * mm, "end": v(145, -57.5) * mm});
            skLineSegment(sketch, "E166.MirrorCS", {"start": v(145, 7.5) * mm, "end": v(145, -7.5) * mm});
            skLineSegment(sketch, "E167.MirrorCS", {"start": v(145, -67.5) * mm, "end": v(145, -82.5) * mm});
            skLineSegment(sketch, "E168.MirrorCS", {"start": v(145, -17.5) * mm, "end": v(145, -32.5) * mm});
            skLineSegment(sketch, "E169.MirrorCS", {"start": v(150, 7.5) * mm, "end": v(150, 17.5) * mm});
            skLineSegment(sketch, "E170.MirrorCS", {"start": v(150, -17.5) * mm, "end": v(150, -7.5) * mm});
            skLineSegment(sketch, "E171.MirrorCS", {"start": v(145, 17.5) * mm, "end": v(145, 32.5) * mm});
            skLineSegment(sketch, "E172.MirrorCS", {"start": v(145, 42.5) * mm, "end": v(145, 57.5) * mm});
            skLineSegment(sketch, "E173.MirrorCS", {"start": v(150, 32.5) * mm, "end": v(150, 42.5) * mm});
            skLineSegment(sketch, "E174.MirrorCS", {"start": v(150, 82.5) * mm, "end": v(150, -82.5) * mm});
            skSolve(sketch);
        }
        {
            var Q0;
            Q0=qSketchRegion(id+"F2",true);
            var Q1;
            Q1=makeQuery(id+"F1.opExtrude","CAP_FACE",FACE,{"disambiguationData":[OSD([sQuery(id+"F0.wireOp",EDGE,"E0.bottom"),sQuery(id+"F0.wireOp",EDGE,"E0.top"),sQuery(id+"F0.wireOp",EDGE,"E0.left"),sQuery(id+"F0.wireOp",EDGE,"E0.right"),sQuery(id+"F0.wireOp",EDGE,"E7.1.0.0"),sQuery(id+"F0.wireOp",EDGE,"E7.1.0.1"),sQuery(id+"F0.wireOp",EDGE,"E7.1.0.2"),sQuery(id+"F0.wireOp",EDGE,"E7.2.0.0"),sQuery(id+"F0.wireOp",EDGE,"E7.2.0.1"),sQuery(id+"F0.wireOp",EDGE,"E7.2.0.2"),sQuery(id+"F0.wireOp",EDGE,"E7.3.0.0"),sQuery(id+"F0.wireOp",EDGE,"E7.3.0.1"),sQuery(id+"F0.wireOp",EDGE,"E7.3.0.2"),sQuery(id+"F0.wireOp",EDGE,"E7.4.0.0"),sQuery(id+"F0.wireOp",EDGE,"E7.4.0.1"),sQuery(id+"F0.wireOp",EDGE,"E7.4.0.2"),sQuery(id+"F0.wireOp",EDGE,"E8.MirrorCS"),sQuery(id+"F0.wireOp",EDGE,"E9.MirrorCS"),sQuery(id+"F0.wireOp",EDGE,"E10.MirrorCS"),sQuery(id+"F0.wireOp",EDGE,"E4"),sQuery(id+"F0.wireOp",EDGE,"E2"),sQuery(id+"F0.wireOp",EDGE,"E11.MirrorCS"),sQuery(id+"F0.wireOp",EDGE,"E12.MirrorCS"),sQuery(id+"F0.wireOp",EDGE,"E13.MirrorCS"),sQuery(id+"F0.wireOp",EDGE,"E14.MirrorCS"),sQuery(id+"F0.wireOp",EDGE,"E15.MirrorCS"),sQuery(id+"F0.wireOp",EDGE,"E16.MirrorCS"),sQuery(id+"F0.wireOp",EDGE,"E17.MirrorCS"),sQuery(id+"F0.wireOp",EDGE,"E18.MirrorCS"),sQuery(id+"F0.wireOp",EDGE,"E20.MirrorCS"),sQuery(id+"F0.wireOp",EDGE,"E21.MirrorCS"),sQuery(id+"F0.wireOp",EDGE,"E25.MirrorCS"),sQuery(id+"F0.wireOp",EDGE,"E22.MirrorCS"),sQuery(id+"F0.wireOp",EDGE,"E26.MirrorCS"),sQuery(id+"F0.wireOp",EDGE,"E27.MirrorCS"),sQuery(id+"F0.wireOp",EDGE,"E28.MirrorCS"),sQuery(id+"F0.wireOp",EDGE,"E29.MirrorCS"),sQuery(id+"F0.wireOp",EDGE,"E30.MirrorCS"),sQuery(id+"F0.wireOp",EDGE,"E31.MirrorCS"),sQuery(id+"F0.wireOp",EDGE,"E32.MirrorCS"),sQuery(id+"F0.wireOp",EDGE,"E33.MirrorCS"),sQuery(id+"F0.wireOp",EDGE,"E34.MirrorCS"),sQuery(id+"F0.wireOp",EDGE,"E35.MirrorCS"),sQuery(id+"F0.wireOp",EDGE,"E37.MirrorCS"),sQuery(id+"F0.wireOp",EDGE,"E38.MirrorCS"),sQuery(id+"F0.wireOp",EDGE,"E39.MirrorCS"),sQuery(id+"F0.wireOp",EDGE,"E40.MirrorCS"),sQuery(id+"F0.wireOp",EDGE,"E41.MirrorCS"),sQuery(id+"F0.wireOp",EDGE,"E42.MirrorCS"),sQuery(id+"F0.wireOp",EDGE,"E43.MirrorCS"),sQuery(id+"F0.wireOp",EDGE,"E44.MirrorCS"),sQuery(id+"F0.wireOp",EDGE,"E45.MirrorCS"),sQuery(id+"F0.wireOp",EDGE,"E46.MirrorCS"),sQuery(id+"F0.wireOp",EDGE,"E47.MirrorCS"),sQuery(id+"F0.wireOp",EDGE,"E48.MirrorCS"),sQuery(id+"F0.wireOp",EDGE,"E49.MirrorCS"),sQuery(id+"F0.wireOp",EDGE,"E50.MirrorCS"),sQuery(id+"F0.wireOp",EDGE,"E51.MirrorCS"),sQuery(id+"F0.wireOp",EDGE,"E54.MirrorCS"),sQuery(id+"F0.wireOp",EDGE,"E59.0.1.0"),sQuery(id+"F0.wireOp",EDGE,"E59.0.1.1"),sQuery(id+"F0.wireOp",EDGE,"E59.0.1.2"),sQuery(id+"F0.wireOp",EDGE,"E59.0.2.0"),sQuery(id+"F0.wireOp",EDGE,"E59.0.2.1"),sQuery(id+"F0.wireOp",EDGE,"E59.0.2.2"),sQuery(id+"F0.wireOp",EDGE,"E59.0.3.0"),sQuery(id+"F0.wireOp",EDGE,"E59.0.3.1"),sQuery(id+"F0.wireOp",EDGE,"E59.0.3.2"),sQuery(id+"F0.wireOp",EDGE,"E60.MirrorCS"),sQuery(id+"F0.wireOp",EDGE,"E56"),sQuery(id+"F0.wireOp",EDGE,"E61.MirrorCS"),sQuery(id+"F0.wireOp",EDGE,"E62.MirrorCS"),sQuery(id+"F0.wireOp",EDGE,"E57"),sQuery(id+"F0.wireOp",EDGE,"E63.MirrorCS"),sQuery(id+"F0.wireOp",EDGE,"E64.MirrorCS"),sQuery(id+"F0.wireOp",EDGE,"E65.MirrorCS"),sQuery(id+"F0.wireOp",EDGE,"E66.MirrorCS"),sQuery(id+"F0.wireOp",EDGE,"E67.MirrorCS"),sQuery(id+"F0.wireOp",EDGE,"E68.MirrorCS"),sQuery(id+"F0.wireOp",EDGE,"E70.MirrorCS"),sQuery(id+"F0.wireOp",EDGE,"E71.MirrorCS"),sQuery(id+"F0.wireOp",EDGE,"E72.MirrorCS"),sQuery(id+"F0.wireOp",EDGE,"E75.MirrorCS"),sQuery(id+"F0.wireOp",EDGE,"E76.MirrorCS"),sQuery(id+"F0.wireOp",EDGE,"E77.MirrorCS"),sQuery(id+"F0.wireOp",EDGE,"E78.MirrorCS"),sQuery(id+"F0.wireOp",EDGE,"E79.MirrorCS"),sQuery(id+"F0.wireOp",EDGE,"E80.MirrorCS"),sQuery(id+"F0.wireOp",EDGE,"E81.MirrorCS"),sQuery(id+"F0.wireOp",EDGE,"E82.MirrorCS"),sQuery(id+"F0.wireOp",EDGE,"E84.MirrorCS"),sQuery(id+"F0.wireOp",EDGE,"E85.MirrorCS"),sQuery(id+"F0.wireOp",EDGE,"E86.MirrorCS"),sQuery(id+"F0.wireOp",EDGE,"E87.MirrorCS"),sQuery(id+"F0.wireOp",EDGE,"E88.MirrorCS"),sQuery(id+"F0.wireOp",EDGE,"E89.MirrorCS"),sQuery(id+"F0.wireOp",EDGE,"E90.MirrorCS"),sQuery(id+"F0.wireOp",EDGE,"E91.MirrorCS"),sQuery(id+"F0.wireOp",EDGE,"E92.MirrorCS"),sQuery(id+"F0.wireOp",EDGE,"E94.MirrorCS"),sQuery(id+"F0.wireOp",EDGE,"E96.MirrorCS")])],"isStart":true});
            extrude(context, id + "F3", {"entities" : qUnion([Q0]), "endBound" : BoundingType.UP_TO_SURFACE, "oppositeDirection" : true, "endBoundEntityFace" : qUnion([Q1]), "depth" : 25 * mm});
        }
        {
            var Q0;
            Q0=makeQuery(id+"F1.opExtrude","CAP_FACE",FACE,{"disambiguationData":[OSD([sQuery(id+"F0.wireOp",EDGE,"E0.bottom"),sQuery(id+"F0.wireOp",EDGE,"E0.top"),sQuery(id+"F0.wireOp",EDGE,"E0.left"),sQuery(id+"F0.wireOp",EDGE,"E0.right"),sQuery(id+"F0.wireOp",EDGE,"E7.1.0.0"),sQuery(id+"F0.wireOp",EDGE,"E7.1.0.1"),sQuery(id+"F0.wireOp",EDGE,"E7.1.0.2"),sQuery(id+"F0.wireOp",EDGE,"E7.2.0.0"),sQuery(id+"F0.wireOp",EDGE,"E7.2.0.1"),sQuery(id+"F0.wireOp",EDGE,"E7.2.0.2"),sQuery(id+"F0.wireOp",EDGE,"E7.3.0.0"),sQuery(id+"F0.wireOp",EDGE,"E7.3.0.1"),sQuery(id+"F0.wireOp",EDGE,"E7.3.0.2"),sQuery(id+"F0.wireOp",EDGE,"E7.4.0.0"),sQuery(id+"F0.wireOp",EDGE,"E7.4.0.1"),sQuery(id+"F0.wireOp",EDGE,"E7.4.0.2"),sQuery(id+"F0.wireOp",EDGE,"E8.MirrorCS"),sQuery(id+"F0.wireOp",EDGE,"E9.MirrorCS"),sQuery(id+"F0.wireOp",EDGE,"E10.MirrorCS"),sQuery(id+"F0.wireOp",EDGE,"E4"),sQuery(id+"F0.wireOp",EDGE,"E2"),sQuery(id+"F0.wireOp",EDGE,"E11.MirrorCS"),sQuery(id+"F0.wireOp",EDGE,"E12.MirrorCS"),sQuery(id+"F0.wireOp",EDGE,"E13.MirrorCS"),sQuery(id+"F0.wireOp",EDGE,"E14.MirrorCS"),sQuery(id+"F0.wireOp",EDGE,"E15.MirrorCS"),sQuery(id+"F0.wireOp",EDGE,"E16.MirrorCS"),sQuery(id+"F0.wireOp",EDGE,"E17.MirrorCS"),sQuery(id+"F0.wireOp",EDGE,"E18.MirrorCS"),sQuery(id+"F0.wireOp",EDGE,"E20.MirrorCS"),sQuery(id+"F0.wireOp",EDGE,"E21.MirrorCS"),sQuery(id+"F0.wireOp",EDGE,"E25.MirrorCS"),sQuery(id+"F0.wireOp",EDGE,"E22.MirrorCS"),sQuery(id+"F0.wireOp",EDGE,"E26.MirrorCS"),sQuery(id+"F0.wireOp",EDGE,"E27.MirrorCS"),sQuery(id+"F0.wireOp",EDGE,"E28.MirrorCS"),sQuery(id+"F0.wireOp",EDGE,"E29.MirrorCS"),sQuery(id+"F0.wireOp",EDGE,"E30.MirrorCS"),sQuery(id+"F0.wireOp",EDGE,"E31.MirrorCS"),sQuery(id+"F0.wireOp",EDGE,"E32.MirrorCS"),sQuery(id+"F0.wireOp",EDGE,"E33.MirrorCS"),sQuery(id+"F0.wireOp",EDGE,"E34.MirrorCS"),sQuery(id+"F0.wireOp",EDGE,"E35.MirrorCS"),sQuery(id+"F0.wireOp",EDGE,"E37.MirrorCS"),sQuery(id+"F0.wireOp",EDGE,"E38.MirrorCS"),sQuery(id+"F0.wireOp",EDGE,"E39.MirrorCS"),sQuery(id+"F0.wireOp",EDGE,"E40.MirrorCS"),sQuery(id+"F0.wireOp",EDGE,"E41.MirrorCS"),sQuery(id+"F0.wireOp",EDGE,"E42.MirrorCS"),sQuery(id+"F0.wireOp",EDGE,"E43.MirrorCS"),sQuery(id+"F0.wireOp",EDGE,"E44.MirrorCS"),sQuery(id+"F0.wireOp",EDGE,"E45.MirrorCS"),sQuery(id+"F0.wireOp",EDGE,"E46.MirrorCS"),sQuery(id+"F0.wireOp",EDGE,"E47.MirrorCS"),sQuery(id+"F0.wireOp",EDGE,"E48.MirrorCS"),sQuery(id+"F0.wireOp",EDGE,"E49.MirrorCS"),sQuery(id+"F0.wireOp",EDGE,"E50.MirrorCS"),sQuery(id+"F0.wireOp",EDGE,"E51.MirrorCS"),sQuery(id+"F0.wireOp",EDGE,"E54.MirrorCS"),sQuery(id+"F0.wireOp",EDGE,"E59.0.1.0"),sQuery(id+"F0.wireOp",EDGE,"E59.0.1.1"),sQuery(id+"F0.wireOp",EDGE,"E59.0.1.2"),sQuery(id+"F0.wireOp",EDGE,"E59.0.2.0"),sQuery(id+"F0.wireOp",EDGE,"E59.0.2.1"),sQuery(id+"F0.wireOp",EDGE,"E59.0.2.2"),sQuery(id+"F0.wireOp",EDGE,"E59.0.3.0"),sQuery(id+"F0.wireOp",EDGE,"E59.0.3.1"),sQuery(id+"F0.wireOp",EDGE,"E59.0.3.2"),sQuery(id+"F0.wireOp",EDGE,"E60.MirrorCS"),sQuery(id+"F0.wireOp",EDGE,"E56"),sQuery(id+"F0.wireOp",EDGE,"E61.MirrorCS"),sQuery(id+"F0.wireOp",EDGE,"E62.MirrorCS"),sQuery(id+"F0.wireOp",EDGE,"E57"),sQuery(id+"F0.wireOp",EDGE,"E63.MirrorCS"),sQuery(id+"F0.wireOp",EDGE,"E64.MirrorCS"),sQuery(id+"F0.wireOp",EDGE,"E65.MirrorCS"),sQuery(id+"F0.wireOp",EDGE,"E66.MirrorCS"),sQuery(id+"F0.wireOp",EDGE,"E67.MirrorCS"),sQuery(id+"F0.wireOp",EDGE,"E68.MirrorCS"),sQuery(id+"F0.wireOp",EDGE,"E70.MirrorCS"),sQuery(id+"F0.wireOp",EDGE,"E71.MirrorCS"),sQuery(id+"F0.wireOp",EDGE,"E72.MirrorCS"),sQuery(id+"F0.wireOp",EDGE,"E75.MirrorCS"),sQuery(id+"F0.wireOp",EDGE,"E76.MirrorCS"),sQuery(id+"F0.wireOp",EDGE,"E77.MirrorCS"),sQuery(id+"F0.wireOp",EDGE,"E78.MirrorCS"),sQuery(id+"F0.wireOp",EDGE,"E79.MirrorCS"),sQuery(id+"F0.wireOp",EDGE,"E80.MirrorCS"),sQuery(id+"F0.wireOp",EDGE,"E81.MirrorCS"),sQuery(id+"F0.wireOp",EDGE,"E82.MirrorCS"),sQuery(id+"F0.wireOp",EDGE,"E84.MirrorCS"),sQuery(id+"F0.wireOp",EDGE,"E85.MirrorCS"),sQuery(id+"F0.wireOp",EDGE,"E86.MirrorCS"),sQuery(id+"F0.wireOp",EDGE,"E87.MirrorCS"),sQuery(id+"F0.wireOp",EDGE,"E88.MirrorCS"),sQuery(id+"F0.wireOp",EDGE,"E89.MirrorCS"),sQuery(id+"F0.wireOp",EDGE,"E90.MirrorCS"),sQuery(id+"F0.wireOp",EDGE,"E91.MirrorCS"),sQuery(id+"F0.wireOp",EDGE,"E92.MirrorCS"),sQuery(id+"F0.wireOp",EDGE,"E94.MirrorCS"),sQuery(id+"F0.wireOp",EDGE,"E96.MirrorCS")])],"isStart":false});
            var sketch = newSketch(context, id + "F4", { "sketchPlane" : qUnion([Q0])});
            skPoint(sketch, "E175.0", {"position": v(127.5, 96) * mm});
            skLineSegment(sketch, "E176.bottom", {"start": v(-150, 100) * mm, "end": v(150, 100) * mm});
            skLineSegment(sketch, "E176.top", {"start": v(-150, 96) * mm, "end": v(150, 96) * mm});
            skLineSegment(sketch, "E176.left", {"start": v(-150, 100) * mm, "end": v(-150, 96) * mm});
            skLineSegment(sketch, "E176.right", {"start": v(150, 100) * mm, "end": v(150, 96) * mm});
            skSolve(sketch);
        }
        {
            var Q0;
            Q0=qSketchRegion(id+"F4",true);
            extrude(context, id + "F5", {"entities" : qUnion([Q0]), "depth" : 96 * mm});
        }
        {
            var Q0;
            Q0=makeQuery(id+"F3.opExtrude","SWEPT_BODY",BODY,{"disambiguationData":[OSD([sQuery(id+"F2.wireOp",EDGE,"E97.59"),sQuery(id+"F2.wireOp",EDGE,"E97.60"),sQuery(id+"F2.wireOp",EDGE,"E97.75"),sQuery(id+"F2.wireOp",EDGE,"E98")])]});
            var Q1;
            Q1=makeQuery(id+"F3.opExtrude","SWEPT_BODY",BODY,{"disambiguationData":[OSD([sQuery(id+"F2.wireOp",EDGE,"E97.47"),sQuery(id+"F2.wireOp",EDGE,"E97.61"),sQuery(id+"F2.wireOp",EDGE,"E97.98"),sQuery(id+"F2.wireOp",EDGE,"E102.trimOffspring")])]});
            var Q2;
            Q2=makeQuery(id+"F3.opExtrude","SWEPT_BODY",BODY,{"disambiguationData":[OSD([sQuery(id+"F2.wireOp",EDGE,"E97.43"),sQuery(id+"F2.wireOp",EDGE,"E97.74"),sQuery(id+"F2.wireOp",EDGE,"E97.87"),sQuery(id+"F2.wireOp",EDGE,"E101.trimOffspring")])]});
            var Q3;
            Q3=makeQuery(id+"F3.opExtrude","SWEPT_BODY",BODY,{"disambiguationData":[OSD([sQuery(id+"F2.wireOp",EDGE,"E97.81"),sQuery(id+"F2.wireOp",EDGE,"E97.90"),sQuery(id+"F2.wireOp",EDGE,"E97.104"),sQuery(id+"F2.wireOp",EDGE,"E100.trimOffspring")])]});
            var Q4;
            Q4=makeQuery(id+"F3.opExtrude","SWEPT_BODY",BODY,{"disambiguationData":[OSD([sQuery(id+"F2.wireOp",EDGE,"E97.56"),sQuery(id+"F2.wireOp",EDGE,"E97.80"),sQuery(id+"F2.wireOp",EDGE,"E97.100"),sQuery(id+"F2.wireOp",EDGE,"E99.trimOffspring")])]});
            var Q5;
            Q5=makeQuery(id+"F3.opExtrude","SWEPT_BODY",BODY,{"disambiguationData":[OSD([sQuery(id+"F2.wireOp",EDGE,"E97.72"),sQuery(id+"F2.wireOp",EDGE,"E97.78"),sQuery(id+"F2.wireOp",EDGE,"E97.85"),sQuery(id+"F2.wireOp",EDGE,"E103.trimOffspring")])]});
            var Q6;
            Q6=makeQuery(id+"F3.opExtrude","SWEPT_BODY",BODY,{"disambiguationData":[OSD([sQuery(id+"F2.wireOp",EDGE,"E97.42"),sQuery(id+"F2.wireOp",EDGE,"E97.50"),sQuery(id+"F2.wireOp",EDGE,"E97.91"),sQuery(id+"F2.wireOp",EDGE,"E103.trimOffspring")])]});
            var Q7;
            Q7=makeQuery(id+"F3.opExtrude","SWEPT_BODY",BODY,{"disambiguationData":[OSD([sQuery(id+"F2.wireOp",EDGE,"E97.48"),sQuery(id+"F2.wireOp",EDGE,"E97.57"),sQuery(id+"F2.wireOp",EDGE,"E97.64"),sQuery(id+"F2.wireOp",EDGE,"E103.trimOffspring")])]});
            var Q8;
            Q8=makeQuery(id+"F3.opExtrude","SWEPT_BODY",BODY,{"disambiguationData":[OSD([sQuery(id+"F2.wireOp",EDGE,"E97.79"),sQuery(id+"F2.wireOp",EDGE,"E97.86"),sQuery(id+"F2.wireOp",EDGE,"E97.92"),sQuery(id+"F2.wireOp",EDGE,"E103.trimOffspring")])]});
            var Q9;
            Q9=makeQuery(id+"F5.opExtrude","SWEPT_BODY",BODY,{"disambiguationData":[OSD([sQuery(id+"F4.wireOp",EDGE,"E176.bottom"),sQuery(id+"F4.wireOp",EDGE,"E176.top"),sQuery(id+"F4.wireOp",EDGE,"E176.left"),sQuery(id+"F4.wireOp",EDGE,"E176.right")])]});
            booleanBodies(context, id + "F6", {"operationType" : BooleanOperationType.UNION, "tools" : qUnion([Q0, Q1, Q2, Q3, Q4, Q5, Q6, Q7, Q8, Q9])});
        }
        {
            var Q0;
            Q0=makeQuery(id+"F3.opExtrude","SWEPT_BODY",BODY,{"disambiguationData":[OSD([sQuery(id+"F2.wireOp",EDGE,"E97.59"),sQuery(id+"F2.wireOp",EDGE,"E97.60"),sQuery(id+"F2.wireOp",EDGE,"E97.75"),sQuery(id+"F2.wireOp",EDGE,"E98")])]});
            var Q1;
            Q1=qCreatedBy(makeId("Front.planeOp"),FACE);
            mirror(context, id + "F7", {"entities" : qUnion([Q0]), "mirrorPlane" : qUnion([Q1])});
        }
        {
            var Q0;
            Q0=makeQuery(id+"F3.opExtrude","SWEPT_BODY",BODY,{"disambiguationData":[OSD([sQuery(id+"F2.wireOp",EDGE,"E105.MirrorCS"),sQuery(id+"F2.wireOp",EDGE,"E117.MirrorCS"),sQuery(id+"F2.wireOp",EDGE,"E135.MirrorCS"),sQuery(id+"F2.wireOp",EDGE,"E122.MirrorCS")])]});
            var Q1;
            Q1=makeQuery(id+"F7.opPattern","COPY",BODY,{"derivedFrom":makeQuery(id+"F3.opExtrude","SWEPT_BODY",BODY,{"disambiguationData":[OSD([sQuery(id+"F2.wireOp",EDGE,"E97.59"),sQuery(id+"F2.wireOp",EDGE,"E97.60"),sQuery(id+"F2.wireOp",EDGE,"E97.75"),sQuery(id+"F2.wireOp",EDGE,"E98")])]}),"instanceName":"1"});
            var Q2;
            Q2=makeQuery(id+"F3.opExtrude","SWEPT_BODY",BODY,{"disambiguationData":[OSD([sQuery(id+"F2.wireOp",EDGE,"E113.MirrorCS"),sQuery(id+"F2.wireOp",EDGE,"E104.MirrorCS"),sQuery(id+"F2.wireOp",EDGE,"E125.MirrorCS"),sQuery(id+"F2.wireOp",EDGE,"E144.MirrorCS")])]});
            var Q3;
            Q3=makeQuery(id+"F3.opExtrude","SWEPT_BODY",BODY,{"disambiguationData":[OSD([sQuery(id+"F2.wireOp",EDGE,"E110.MirrorCS"),sQuery(id+"F2.wireOp",EDGE,"E108.MirrorCS"),sQuery(id+"F2.wireOp",EDGE,"E137.MirrorCS"),sQuery(id+"F2.wireOp",EDGE,"E128.MirrorCS")])]});
            var Q4;
            Q4=makeQuery(id+"F3.opExtrude","SWEPT_BODY",BODY,{"disambiguationData":[OSD([sQuery(id+"F2.wireOp",EDGE,"E111.MirrorCS"),sQuery(id+"F2.wireOp",EDGE,"E112.MirrorCS"),sQuery(id+"F2.wireOp",EDGE,"E142.MirrorCS"),sQuery(id+"F2.wireOp",EDGE,"E129.MirrorCS")])]});
            var Q5;
            Q5=makeQuery(id+"F3.opExtrude","SWEPT_BODY",BODY,{"disambiguationData":[OSD([sQuery(id+"F2.wireOp",EDGE,"E109.MirrorCS"),sQuery(id+"F2.wireOp",EDGE,"E106.MirrorCS"),sQuery(id+"F2.wireOp",EDGE,"E134.MirrorCS"),sQuery(id+"F2.wireOp",EDGE,"E126.MirrorCS")])]});
            var Q6;
            Q6=makeQuery(id+"F3.opExtrude","SWEPT_BODY",BODY,{"disambiguationData":[OSD([sQuery(id+"F2.wireOp",EDGE,"E107.MirrorCS"),sQuery(id+"F2.wireOp",EDGE,"E114.MirrorCS"),sQuery(id+"F2.wireOp",EDGE,"E123.MirrorCS"),sQuery(id+"F2.wireOp",EDGE,"E140.MirrorCS")])]});
            var Q7;
            Q7=makeQuery(id+"F3.opExtrude","SWEPT_BODY",BODY,{"disambiguationData":[OSD([sQuery(id+"F2.wireOp",EDGE,"E115.MirrorCS"),sQuery(id+"F2.wireOp",EDGE,"E121.MirrorCS"),sQuery(id+"F2.wireOp",EDGE,"E140.MirrorCS"),sQuery(id+"F2.wireOp",EDGE,"E133.MirrorCS")])]});
            var Q8;
            Q8=makeQuery(id+"F3.opExtrude","SWEPT_BODY",BODY,{"disambiguationData":[OSD([sQuery(id+"F2.wireOp",EDGE,"E116.MirrorCS"),sQuery(id+"F2.wireOp",EDGE,"E118.MirrorCS"),sQuery(id+"F2.wireOp",EDGE,"E140.MirrorCS"),sQuery(id+"F2.wireOp",EDGE,"E124.MirrorCS")])]});
            var Q9;
            Q9=makeQuery(id+"F3.opExtrude","SWEPT_BODY",BODY,{"disambiguationData":[OSD([sQuery(id+"F2.wireOp",EDGE,"E120.MirrorCS"),sQuery(id+"F2.wireOp",EDGE,"E119.MirrorCS"),sQuery(id+"F2.wireOp",EDGE,"E140.MirrorCS"),sQuery(id+"F2.wireOp",EDGE,"E127.MirrorCS")])]});
            booleanBodies(context, id + "F8", {"operationType" : BooleanOperationType.UNION, "tools" : qUnion([Q0, Q1, Q2, Q3, Q4, Q5, Q6, Q7, Q8, Q9])});
        }
        {
            var Q0;
            Q0=makeQuery(id+"F1.opExtrude","CAP_FACE",FACE,{"disambiguationData":[OSD([sQuery(id+"F0.wireOp",EDGE,"E0.bottom"),sQuery(id+"F0.wireOp",EDGE,"E0.top"),sQuery(id+"F0.wireOp",EDGE,"E0.left"),sQuery(id+"F0.wireOp",EDGE,"E0.right"),sQuery(id+"F0.wireOp",EDGE,"E7.1.0.0"),sQuery(id+"F0.wireOp",EDGE,"E7.1.0.1"),sQuery(id+"F0.wireOp",EDGE,"E7.1.0.2"),sQuery(id+"F0.wireOp",EDGE,"E7.2.0.0"),sQuery(id+"F0.wireOp",EDGE,"E7.2.0.1"),sQuery(id+"F0.wireOp",EDGE,"E7.2.0.2"),sQuery(id+"F0.wireOp",EDGE,"E7.3.0.0"),sQuery(id+"F0.wireOp",EDGE,"E7.3.0.1"),sQuery(id+"F0.wireOp",EDGE,"E7.3.0.2"),sQuery(id+"F0.wireOp",EDGE,"E7.4.0.0"),sQuery(id+"F0.wireOp",EDGE,"E7.4.0.1"),sQuery(id+"F0.wireOp",EDGE,"E7.4.0.2"),sQuery(id+"F0.wireOp",EDGE,"E8.MirrorCS"),sQuery(id+"F0.wireOp",EDGE,"E9.MirrorCS"),sQuery(id+"F0.wireOp",EDGE,"E10.MirrorCS"),sQuery(id+"F0.wireOp",EDGE,"E4"),sQuery(id+"F0.wireOp",EDGE,"E2"),sQuery(id+"F0.wireOp",EDGE,"E11.MirrorCS"),sQuery(id+"F0.wireOp",EDGE,"E12.MirrorCS"),sQuery(id+"F0.wireOp",EDGE,"E13.MirrorCS"),sQuery(id+"F0.wireOp",EDGE,"E14.MirrorCS"),sQuery(id+"F0.wireOp",EDGE,"E15.MirrorCS"),sQuery(id+"F0.wireOp",EDGE,"E16.MirrorCS"),sQuery(id+"F0.wireOp",EDGE,"E17.MirrorCS"),sQuery(id+"F0.wireOp",EDGE,"E18.MirrorCS"),sQuery(id+"F0.wireOp",EDGE,"E20.MirrorCS"),sQuery(id+"F0.wireOp",EDGE,"E21.MirrorCS"),sQuery(id+"F0.wireOp",EDGE,"E25.MirrorCS"),sQuery(id+"F0.wireOp",EDGE,"E22.MirrorCS"),sQuery(id+"F0.wireOp",EDGE,"E26.MirrorCS"),sQuery(id+"F0.wireOp",EDGE,"E27.MirrorCS"),sQuery(id+"F0.wireOp",EDGE,"E28.MirrorCS"),sQuery(id+"F0.wireOp",EDGE,"E29.MirrorCS"),sQuery(id+"F0.wireOp",EDGE,"E30.MirrorCS"),sQuery(id+"F0.wireOp",EDGE,"E31.MirrorCS"),sQuery(id+"F0.wireOp",EDGE,"E32.MirrorCS"),sQuery(id+"F0.wireOp",EDGE,"E33.MirrorCS"),sQuery(id+"F0.wireOp",EDGE,"E34.MirrorCS"),sQuery(id+"F0.wireOp",EDGE,"E35.MirrorCS"),sQuery(id+"F0.wireOp",EDGE,"E37.MirrorCS"),sQuery(id+"F0.wireOp",EDGE,"E38.MirrorCS"),sQuery(id+"F0.wireOp",EDGE,"E39.MirrorCS"),sQuery(id+"F0.wireOp",EDGE,"E40.MirrorCS"),sQuery(id+"F0.wireOp",EDGE,"E41.MirrorCS"),sQuery(id+"F0.wireOp",EDGE,"E42.MirrorCS"),sQuery(id+"F0.wireOp",EDGE,"E43.MirrorCS"),sQuery(id+"F0.wireOp",EDGE,"E44.MirrorCS"),sQuery(id+"F0.wireOp",EDGE,"E45.MirrorCS"),sQuery(id+"F0.wireOp",EDGE,"E46.MirrorCS"),sQuery(id+"F0.wireOp",EDGE,"E47.MirrorCS"),sQuery(id+"F0.wireOp",EDGE,"E48.MirrorCS"),sQuery(id+"F0.wireOp",EDGE,"E49.MirrorCS"),sQuery(id+"F0.wireOp",EDGE,"E50.MirrorCS"),sQuery(id+"F0.wireOp",EDGE,"E51.MirrorCS"),sQuery(id+"F0.wireOp",EDGE,"E54.MirrorCS"),sQuery(id+"F0.wireOp",EDGE,"E59.0.1.0"),sQuery(id+"F0.wireOp",EDGE,"E59.0.1.1"),sQuery(id+"F0.wireOp",EDGE,"E59.0.1.2"),sQuery(id+"F0.wireOp",EDGE,"E59.0.2.0"),sQuery(id+"F0.wireOp",EDGE,"E59.0.2.1"),sQuery(id+"F0.wireOp",EDGE,"E59.0.2.2"),sQuery(id+"F0.wireOp",EDGE,"E59.0.3.0"),sQuery(id+"F0.wireOp",EDGE,"E59.0.3.1"),sQuery(id+"F0.wireOp",EDGE,"E59.0.3.2"),sQuery(id+"F0.wireOp",EDGE,"E60.MirrorCS"),sQuery(id+"F0.wireOp",EDGE,"E56"),sQuery(id+"F0.wireOp",EDGE,"E61.MirrorCS"),sQuery(id+"F0.wireOp",EDGE,"E62.MirrorCS"),sQuery(id+"F0.wireOp",EDGE,"E57"),sQuery(id+"F0.wireOp",EDGE,"E63.MirrorCS"),sQuery(id+"F0.wireOp",EDGE,"E64.MirrorCS"),sQuery(id+"F0.wireOp",EDGE,"E65.MirrorCS"),sQuery(id+"F0.wireOp",EDGE,"E66.MirrorCS"),sQuery(id+"F0.wireOp",EDGE,"E67.MirrorCS"),sQuery(id+"F0.wireOp",EDGE,"E68.MirrorCS"),sQuery(id+"F0.wireOp",EDGE,"E70.MirrorCS"),sQuery(id+"F0.wireOp",EDGE,"E71.MirrorCS"),sQuery(id+"F0.wireOp",EDGE,"E72.MirrorCS"),sQuery(id+"F0.wireOp",EDGE,"E75.MirrorCS"),sQuery(id+"F0.wireOp",EDGE,"E76.MirrorCS"),sQuery(id+"F0.wireOp",EDGE,"E77.MirrorCS"),sQuery(id+"F0.wireOp",EDGE,"E78.MirrorCS"),sQuery(id+"F0.wireOp",EDGE,"E79.MirrorCS"),sQuery(id+"F0.wireOp",EDGE,"E80.MirrorCS"),sQuery(id+"F0.wireOp",EDGE,"E81.MirrorCS"),sQuery(id+"F0.wireOp",EDGE,"E82.MirrorCS"),sQuery(id+"F0.wireOp",EDGE,"E84.MirrorCS"),sQuery(id+"F0.wireOp",EDGE,"E85.MirrorCS"),sQuery(id+"F0.wireOp",EDGE,"E86.MirrorCS"),sQuery(id+"F0.wireOp",EDGE,"E87.MirrorCS"),sQuery(id+"F0.wireOp",EDGE,"E88.MirrorCS"),sQuery(id+"F0.wireOp",EDGE,"E89.MirrorCS"),sQuery(id+"F0.wireOp",EDGE,"E90.MirrorCS"),sQuery(id+"F0.wireOp",EDGE,"E91.MirrorCS"),sQuery(id+"F0.wireOp",EDGE,"E92.MirrorCS"),sQuery(id+"F0.wireOp",EDGE,"E94.MirrorCS"),sQuery(id+"F0.wireOp",EDGE,"E96.MirrorCS")])],"isStart":false});
            var sketch = newSketch(context, id + "F9", { "sketchPlane" : qUnion([Q0])});
            skLineSegment(sketch, "E177.0", {"start": v(145, 7.5) * mm, "end": v(150, 7.5) * mm});
            skLineSegment(sketch, "E177.1", {"start": v(145, -42.5) * mm, "end": v(150, -42.5) * mm});
            skLineSegment(sketch, "E177.2", {"start": v(145, -17.5) * mm, "end": v(150, -17.5) * mm});
            skLineSegment(sketch, "E177.3", {"start": v(145, 82.5) * mm, "end": v(150, 82.5) * mm});
            skLineSegment(sketch, "E177.4", {"start": v(145, 57.5) * mm, "end": v(150, 57.5) * mm});
            skLineSegment(sketch, "E177.5", {"start": v(145, 32.5) * mm, "end": v(150, 32.5) * mm});
            skLineSegment(sketch, "E177.6", {"start": v(145, -67.5) * mm, "end": v(150, -67.5) * mm});
            skPoint(sketch, "E178.0", {"position": v(150, -96) * mm});
            skPoint(sketch, "E179.0", {"position": v(150, 96) * mm});
            skLineSegment(sketch, "E180.bottom", {"start": v(150, -96) * mm, "end": v(145, -96) * mm});
            skLineSegment(sketch, "E180.top", {"start": v(150, 96) * mm, "end": v(145, 96) * mm});
            skLineSegment(sketch, "E180.left", {"start": v(150, -96) * mm, "end": v(150, 96) * mm});
            skLineSegment(sketch, "E180.right", {"start": v(145, -96) * mm, "end": v(145, 96) * mm});
            skLineSegment(sketch, "E181.MirrorCS", {"start": v(-150, 96) * mm, "end": v(-145, 96) * mm});
            skLineSegment(sketch, "E182.MirrorCS", {"start": v(-150, -96) * mm, "end": v(-145, -96) * mm});
            skLineSegment(sketch, "E183.MirrorCS", {"start": v(-145, 57.5) * mm, "end": v(-150, 57.5) * mm});
            skLineSegment(sketch, "E184.MirrorCS", {"start": v(-145, -42.5) * mm, "end": v(-150, -42.5) * mm});
            skLineSegment(sketch, "E185.MirrorCS", {"start": v(-145, -17.5) * mm, "end": v(-150, -17.5) * mm});
            skLineSegment(sketch, "E186.MirrorCS", {"start": v(-145, 32.5) * mm, "end": v(-150, 32.5) * mm});
            skLineSegment(sketch, "E187.MirrorCS", {"start": v(-145, 7.5) * mm, "end": v(-150, 7.5) * mm});
            skLineSegment(sketch, "E188.MirrorCS", {"start": v(-145, -67.5) * mm, "end": v(-150, -67.5) * mm});
            skLineSegment(sketch, "E189.MirrorCS", {"start": v(-145, 82.5) * mm, "end": v(-150, 82.5) * mm});
            skLineSegment(sketch, "E190.MirrorCS", {"start": v(-145, -96) * mm, "end": v(-145, 96) * mm});
            skPoint(sketch, "E191.MirrorP", {"position": v(-150, 96) * mm});
            skPoint(sketch, "E192.MirrorP", {"position": v(-150, -96) * mm});
            skLineSegment(sketch, "E193.MirrorCS", {"start": v(-150, -96) * mm, "end": v(-150, 96) * mm});
            skSolve(sketch);
        }
        {
            var Q0;
            Q0=qSketchRegion(id+"F9",true);
            extrude(context, id + "F10", {"entities" : qUnion([Q0]), "depth" : 96 * mm});
        }
        {
            var Q0;
            Q0=makeQuery(id+"F3.opExtrude","SWEPT_BODY",BODY,{"disambiguationData":[OSD([sQuery(id+"F2.wireOp",EDGE,"E153.MirrorCS"),sQuery(id+"F2.wireOp",EDGE,"E160.MirrorCS"),sQuery(id+"F2.wireOp",EDGE,"E167.MirrorCS"),sQuery(id+"F2.wireOp",EDGE,"E174.MirrorCS")])]});
            var Q1;
            Q1=makeQuery(id+"F10.opExtrude","SWEPT_BODY",BODY,{"disambiguationData":[OSD([sQuery(id+"F9.wireOp",EDGE,"E180.bottom"),sQuery(id+"F9.wireOp",EDGE,"E180.top"),sQuery(id+"F9.wireOp",EDGE,"E180.left"),sQuery(id+"F9.wireOp",EDGE,"E180.right")])]});
            var Q2;
            Q2=makeQuery(id+"F3.opExtrude","SWEPT_BODY",BODY,{"disambiguationData":[OSD([sQuery(id+"F2.wireOp",EDGE,"E147.MirrorCS"),sQuery(id+"F2.wireOp",EDGE,"E154.MirrorCS"),sQuery(id+"F2.wireOp",EDGE,"E165.MirrorCS"),sQuery(id+"F2.wireOp",EDGE,"E174.MirrorCS")])]});
            var Q3;
            Q3=makeQuery(id+"F3.opExtrude","SWEPT_BODY",BODY,{"disambiguationData":[OSD([sQuery(id+"F2.wireOp",EDGE,"E152.MirrorCS"),sQuery(id+"F2.wireOp",EDGE,"E150.MirrorCS"),sQuery(id+"F2.wireOp",EDGE,"E168.MirrorCS"),sQuery(id+"F2.wireOp",EDGE,"E174.MirrorCS")])]});
            var Q4;
            Q4=makeQuery(id+"F3.opExtrude","SWEPT_BODY",BODY,{"disambiguationData":[OSD([sQuery(id+"F2.wireOp",EDGE,"E157.MirrorCS"),sQuery(id+"F2.wireOp",EDGE,"E158.MirrorCS"),sQuery(id+"F2.wireOp",EDGE,"E166.MirrorCS"),sQuery(id+"F2.wireOp",EDGE,"E174.MirrorCS")])]});
            var Q5;
            Q5=makeQuery(id+"F3.opExtrude","SWEPT_BODY",BODY,{"disambiguationData":[OSD([sQuery(id+"F2.wireOp",EDGE,"E149.MirrorCS"),sQuery(id+"F2.wireOp",EDGE,"E148.MirrorCS"),sQuery(id+"F2.wireOp",EDGE,"E171.MirrorCS"),sQuery(id+"F2.wireOp",EDGE,"E174.MirrorCS")])]});
            var Q6;
            Q6=makeQuery(id+"F3.opExtrude","SWEPT_BODY",BODY,{"disambiguationData":[OSD([sQuery(id+"F2.wireOp",EDGE,"E155.MirrorCS"),sQuery(id+"F2.wireOp",EDGE,"E156.MirrorCS"),sQuery(id+"F2.wireOp",EDGE,"E172.MirrorCS"),sQuery(id+"F2.wireOp",EDGE,"E174.MirrorCS")])]});
            var Q7;
            Q7=makeQuery(id+"F3.opExtrude","SWEPT_BODY",BODY,{"disambiguationData":[OSD([sQuery(id+"F2.wireOp",EDGE,"E151.MirrorCS"),sQuery(id+"F2.wireOp",EDGE,"E159.MirrorCS"),sQuery(id+"F2.wireOp",EDGE,"E164.MirrorCS"),sQuery(id+"F2.wireOp",EDGE,"E174.MirrorCS")])]});
            booleanBodies(context, id + "F11", {"operationType" : BooleanOperationType.UNION, "tools" : qUnion([Q0, Q1, Q2, Q3, Q4, Q5, Q6, Q7])});
        }
        {
            var Q0;
            Q0=makeQuery(id+"F3.opExtrude","SWEPT_BODY",BODY,{"disambiguationData":[OSD([sQuery(id+"F2.wireOp",EDGE,"E145.32"),sQuery(id+"F2.wireOp",EDGE,"E145.33"),sQuery(id+"F2.wireOp",EDGE,"E145.76"),sQuery(id+"F2.wireOp",EDGE,"E146")])]});
            var Q1;
            Q1=makeQuery(id+"F10.opExtrude","SWEPT_BODY",BODY,{"disambiguationData":[OSD([sQuery(id+"F9.wireOp",EDGE,"E181.MirrorCS"),sQuery(id+"F9.wireOp",EDGE,"E182.MirrorCS"),sQuery(id+"F9.wireOp",EDGE,"E190.MirrorCS"),sQuery(id+"F9.wireOp",EDGE,"E193.MirrorCS")])]});
            var Q2;
            Q2=makeQuery(id+"F3.opExtrude","SWEPT_BODY",BODY,{"disambiguationData":[OSD([sQuery(id+"F2.wireOp",EDGE,"E145.54"),sQuery(id+"F2.wireOp",EDGE,"E145.62"),sQuery(id+"F2.wireOp",EDGE,"E145.65"),sQuery(id+"F2.wireOp",EDGE,"E146")])]});
            var Q3;
            Q3=makeQuery(id+"F3.opExtrude","SWEPT_BODY",BODY,{"disambiguationData":[OSD([sQuery(id+"F2.wireOp",EDGE,"E145.35"),sQuery(id+"F2.wireOp",EDGE,"E145.44"),sQuery(id+"F2.wireOp",EDGE,"E145.45"),sQuery(id+"F2.wireOp",EDGE,"E146")])]});
            var Q4;
            Q4=makeQuery(id+"F3.opExtrude","SWEPT_BODY",BODY,{"disambiguationData":[OSD([sQuery(id+"F2.wireOp",EDGE,"E145.47"),sQuery(id+"F2.wireOp",EDGE,"E145.51"),sQuery(id+"F2.wireOp",EDGE,"E145.66"),sQuery(id+"F2.wireOp",EDGE,"E146")])]});
            var Q5;
            Q5=makeQuery(id+"F3.opExtrude","SWEPT_BODY",BODY,{"disambiguationData":[OSD([sQuery(id+"F2.wireOp",EDGE,"E145.34"),sQuery(id+"F2.wireOp",EDGE,"E145.49"),sQuery(id+"F2.wireOp",EDGE,"E145.53"),sQuery(id+"F2.wireOp",EDGE,"E146")])]});
            var Q6;
            Q6=makeQuery(id+"F3.opExtrude","SWEPT_BODY",BODY,{"disambiguationData":[OSD([sQuery(id+"F2.wireOp",EDGE,"E145.75"),sQuery(id+"F2.wireOp",EDGE,"E145.80"),sQuery(id+"F2.wireOp",EDGE,"E145.81"),sQuery(id+"F2.wireOp",EDGE,"E146")])]});
            var Q7;
            Q7=makeQuery(id+"F3.opExtrude","SWEPT_BODY",BODY,{"disambiguationData":[OSD([sQuery(id+"F2.wireOp",EDGE,"E145.37"),sQuery(id+"F2.wireOp",EDGE,"E145.55"),sQuery(id+"F2.wireOp",EDGE,"E145.61"),sQuery(id+"F2.wireOp",EDGE,"E146")])]});
            booleanBodies(context, id + "F12", {"operationType" : BooleanOperationType.UNION, "tools" : qUnion([Q0, Q1, Q2, Q3, Q4, Q5, Q6, Q7])});
        }
    });
